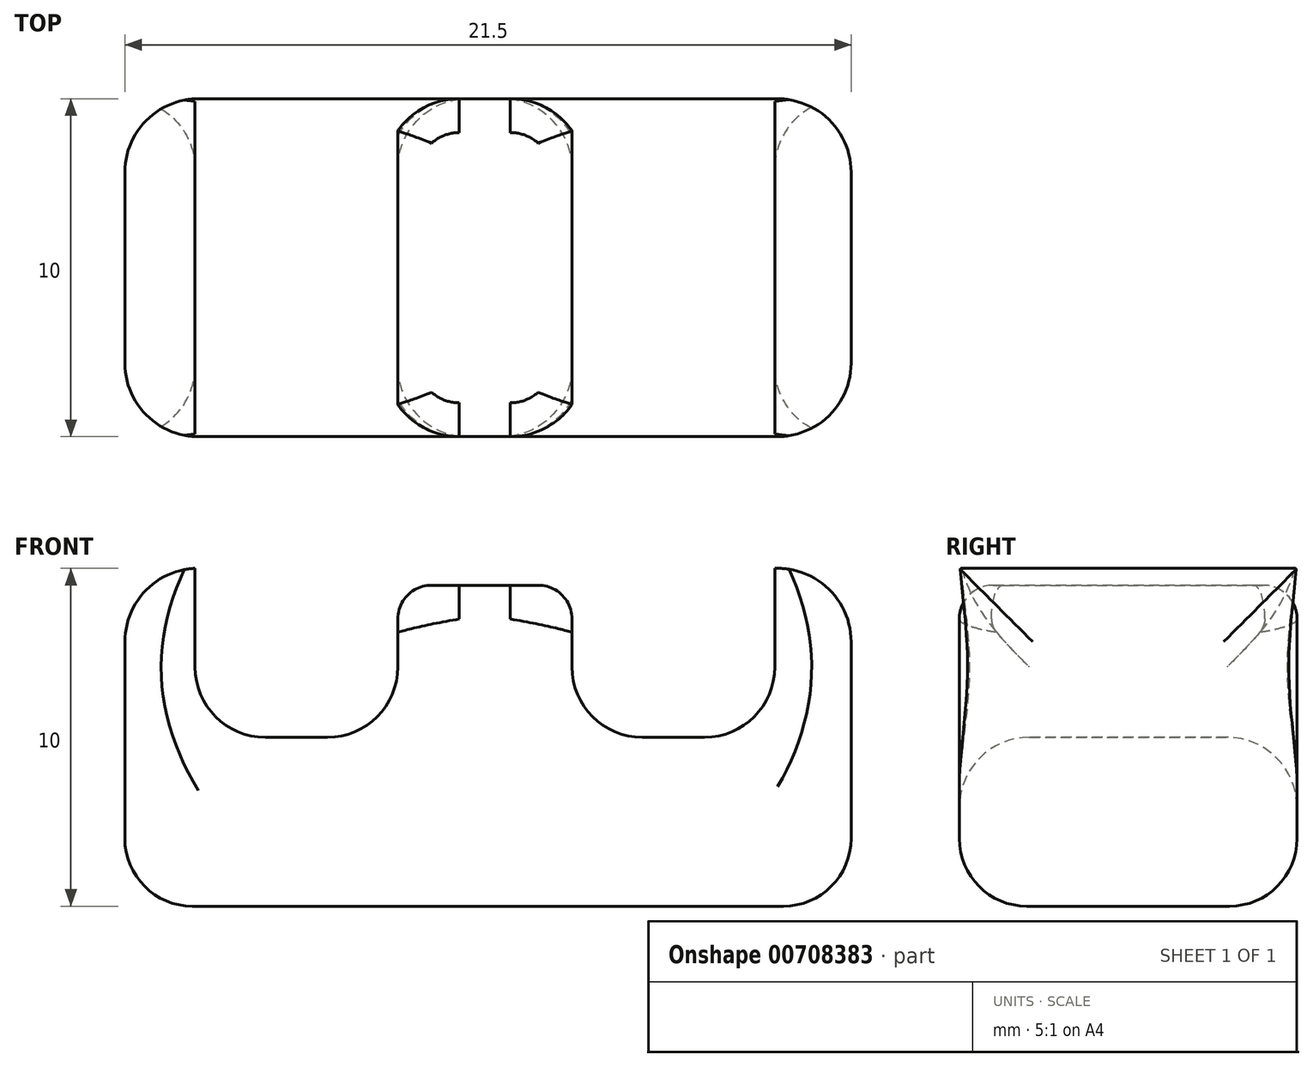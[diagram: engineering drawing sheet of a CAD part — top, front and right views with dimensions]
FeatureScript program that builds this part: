
annotation { "Feature Type Name" : "Feature", "Feature Type Description" : "" }
export const myFeature = defineFeature(function(context is Context, id is Id, definition is map)
    precondition{}
    {
        {
            var Q0;
            Q0=qCreatedBy(makeId("Top.planeOp"),FACE);
            var sketch = newSketch(context, id + "F0", { "sketchPlane" : qUnion([Q0])});
            skLineSegment(sketch, "E0.bottom", {"start": v(-10.73, 4.5) * mm, "end": v(12.77, 4.5) * mm});
            skLineSegment(sketch, "E0.top", {"start": v(-10.73, -5.5) * mm, "end": v(12.77, -5.5) * mm});
            skLineSegment(sketch, "E0.left", {"start": v(-10.73, 4.5) * mm, "end": v(-10.73, -5.5) * mm});
            skLineSegment(sketch, "E0.right", {"start": v(12.77, 4.5) * mm, "end": v(12.77, -5.5) * mm});
            skSolve(sketch);
        }
        {
            var Q0;
            Q0=makeQuery(id+"F0.imprint","IMPRINT",FACE,{"disambiguationData":[TD([[makeQuery(id+"F0.imprint","IMPRINT",EDGE,{"derivedFrom":sQuery(id+"F0.wireOp",EDGE,"E0.bottom")}),-1.0]])]});
            extrude(context, id + "F1", {"entities" : qUnion([Q0]), "depth" : 10 * mm, "offsetDistance" : 25 * mm});
        }
        {
            var Q0;
            Q0=makeQuery(id+"F1.opExtrude","SWEPT_FACE",FACE,{"disambiguationData":[OSD([sQuery(id+"F0.wireOp",EDGE,"E0.left")])]});
            extrude(context, id + "F2", {"entities" : qUnion([Q0]), "operationType" : NewBodyOperationType.REMOVE, "oppositeDirection" : true, "depth" : 2 * mm, "offsetDistance" : 25 * mm});
        }
        {
            var Q0;
            Q0=makeQuery(id+"F1.opExtrude","CAP_FACE",FACE,{"disambiguationData":[OSD([sQuery(id+"F0.wireOp",EDGE,"E0.bottom"),sQuery(id+"F0.wireOp",EDGE,"E0.top"),sQuery(id+"F0.wireOp",EDGE,"E0.left"),sQuery(id+"F0.wireOp",EDGE,"E0.right")])],"isStart":false});
            var sketch = newSketch(context, id + "F3", { "sketchPlane" : qUnion([Q0])});
            skLineSegment(sketch, "E1", {"start": v(-8.73, 1.42) * mm, "end": v(-6.73, 1.42) * mm});
            skLineSegment(sketch, "E2.bottom", {"start": v(-6.66, 4.5) * mm, "end": v(-0.66, 4.5) * mm});
            skLineSegment(sketch, "E2.top", {"start": v(-6.66, -5.5) * mm, "end": v(-0.66, -5.5) * mm});
            skLineSegment(sketch, "E2.left", {"start": v(-6.66, 4.5) * mm, "end": v(-6.66, -5.5) * mm});
            skLineSegment(sketch, "E2.right", {"start": v(-0.66, 4.5) * mm, "end": v(-0.66, -5.5) * mm});
            skSolve(sketch);
        }
        {
            var Q0;
            Q0=makeQuery(id+"F3.imprint","IMPRINT",FACE,{"disambiguationData":[TD([[makeQuery(id+"F3.imprint","IMPRINT",EDGE,{"derivedFrom":sQuery(id+"F3.wireOp",EDGE,"E2.bottom")}),-1.0]])]});
            extrude(context, id + "F4", {"entities" : qUnion([Q0]), "operationType" : NewBodyOperationType.REMOVE, "oppositeDirection" : true, "depth" : 5 * mm, "offsetDistance" : 25 * mm});
        }
        {
            var Q0;
            {var subQ0=sQuery(id+"F0.wireOp",EDGE,"E0.bottom");var subQ1=sQuery(id+"F0.wireOp",EDGE,"E0.right");var subQ2=sQuery(id+"F0.wireOp",EDGE,"E0.top");Q0=makeQuery(id+"F4.boolean.opBoolean","SPLIT",FACE,{"disambiguationData":[TD([makeQuery(id+"F1.opExtrude","SWEPT_FACE",FACE,{"disambiguationData":[OSD([subQ1])]})])],"derivedFrom":makeQuery(id+"F1.opExtrude","CAP_FACE",FACE,{"disambiguationData":[OSD([subQ0,subQ2,sQuery(id+"F0.wireOp",EDGE,"E0.left"),subQ1])],"isStart":false})});}
            var sketch = newSketch(context, id + "F5", { "sketchPlane" : qUnion([Q0])});
            skLineSegment(sketch, "E3.bottom", {"start": v(4.5, -5.5) * mm, "end": v(10.5, -5.5) * mm});
            skLineSegment(sketch, "E3.top", {"start": v(4.5, 4.5) * mm, "end": v(10.5, 4.5) * mm});
            skLineSegment(sketch, "E3.left", {"start": v(4.5, -5.5) * mm, "end": v(4.5, 4.5) * mm});
            skLineSegment(sketch, "E3.right", {"start": v(10.5, -5.5) * mm, "end": v(10.5, 4.5) * mm});
            skSolve(sketch);
        }
        {
            var Q0;
            Q0=makeQuery(id+"F5.imprint","IMPRINT",FACE,{"disambiguationData":[TD([[makeQuery(id+"F5.imprint","IMPRINT",EDGE,{"derivedFrom":sQuery(id+"F5.wireOp",EDGE,"E3.bottom")}),1.0]])]});
            extrude(context, id + "F6", {"entities" : qUnion([Q0]), "operationType" : NewBodyOperationType.REMOVE, "oppositeDirection" : true, "depth" : 5 * mm, "offsetDistance" : 25 * mm});
        }
        {
            var Q0;
            Q0=makeQuery(id+"F6.boolean.opBoolean","COPY",FACE,{"derivedFrom":makeQuery(id+"F6.opExtrude","CAP_FACE",FACE,{"disambiguationData":[OSD([sQuery(id+"F5.wireOp",EDGE,"E3.bottom"),sQuery(id+"F5.wireOp",EDGE,"E3.top"),sQuery(id+"F5.wireOp",EDGE,"E3.left"),sQuery(id+"F5.wireOp",EDGE,"E3.right")])],"isStart":false})});
            fillet(context, id + "F7", {"entities" : qUnion([Q0]), "radius" : 2.08 * mm, "tangentPropagation" : true, "allowEdgeOverflow" : false});
        }
        {
            var Q0;
            Q0=makeQuery(id+"F4.boolean.opBoolean","COPY",FACE,{"derivedFrom":makeQuery(id+"F4.opExtrude","CAP_FACE",FACE,{"disambiguationData":[OSD([sQuery(id+"F3.wireOp",EDGE,"E2.bottom"),sQuery(id+"F3.wireOp",EDGE,"E2.top"),sQuery(id+"F3.wireOp",EDGE,"E2.left"),sQuery(id+"F3.wireOp",EDGE,"E2.right")])],"isStart":false})});
            fillet(context, id + "F8", {"entities" : qUnion([Q0]), "radius" : 2.08 * mm, "tangentPropagation" : true, "allowEdgeOverflow" : false});
        }
        {
            var Q0;
            {var subQ0=sQuery(id+"F0.wireOp",EDGE,"E0.bottom");var subQ2=sQuery(id+"F0.wireOp",EDGE,"E0.top");var subQ4=makeQuery(id+"F4.opExtrude","SWEPT_FACE",FACE,{"disambiguationData":[OSD([sQuery(id+"F3.wireOp",EDGE,"E2.right")])]});var subQ5=sQuery(id+"F0.wireOp",EDGE,"E0.right");Q0=makeQuery(id+"F6.boolean.opBoolean","SPLIT",FACE,{"disambiguationData":[TD([makeQuery(id+"F4.boolean.opBoolean","COPY",FACE,{"derivedFrom":subQ4})])],"derivedFrom":makeQuery(id+"F4.boolean.opBoolean","SPLIT",FACE,{"disambiguationData":[TD([makeQuery(id+"F1.opExtrude","SWEPT_FACE",FACE,{"disambiguationData":[OSD([subQ5])]})])],"derivedFrom":makeQuery(id+"F1.opExtrude","CAP_FACE",FACE,{"disambiguationData":[OSD([subQ0,subQ2,sQuery(id+"F0.wireOp",EDGE,"E0.left"),subQ5])],"isStart":false})})});}
            extrude(context, id + "F9", {"entities" : qUnion([Q0]), "operationType" : NewBodyOperationType.REMOVE, "oppositeDirection" : true, "depth" : 0.5 * mm, "offsetDistance" : 25 * mm});
        }
        {
            var Q0;
            Q0=makeQuery(id+"F1.opExtrude","CAP_FACE",FACE,{"disambiguationData":[OSD([sQuery(id+"F0.wireOp",EDGE,"E0.bottom"),sQuery(id+"F0.wireOp",EDGE,"E0.top"),sQuery(id+"F0.wireOp",EDGE,"E0.left"),sQuery(id+"F0.wireOp",EDGE,"E0.right")])],"isStart":true});
            fillet(context, id + "F10", {"entities" : qUnion([Q0]), "radius" : 2 * mm, "tangentPropagation" : true, "allowEdgeOverflow" : false});
        }
        {
            var Q0;
            Q0=makeQuery(id+"F2.boolean.opBoolean","COPY",FACE,{"derivedFrom":makeQuery(id+"F2.opExtrude","CAP_FACE",FACE,{"disambiguationData":[OSD([sQuery(id+"F0.wireOp",EDGE,"E0.left")])],"isStart":false})});
            fillet(context, id + "F11", {"entities" : qUnion([Q0]), "radius" : 2.17 * mm, "tangentPropagation" : true, "allowEdgeOverflow" : false});
        }
        {
            var Q0;
            Q0=makeQuery(id+"F1.opExtrude","SWEPT_FACE",FACE,{"disambiguationData":[OSD([sQuery(id+"F0.wireOp",EDGE,"E0.right")])]});
            fillet(context, id + "F12", {"entities" : qUnion([Q0]), "radius" : 2.17 * mm, "tangentPropagation" : true, "allowEdgeOverflow" : false});
        }
        {
            var Q0;
            Q0=makeQuery(id+"F9.boolean.opBoolean","COPY",FACE,{"derivedFrom":makeQuery(id+"F9.opExtrude","CAP_FACE",FACE,{"disambiguationData":[OSD([sQuery(id+"F0.wireOp",EDGE,"E0.bottom"),sQuery(id+"F0.wireOp",EDGE,"E0.top"),sQuery(id+"F0.wireOp",EDGE,"E0.left"),sQuery(id+"F0.wireOp",EDGE,"E0.right")])],"isStart":false})});
            fillet(context, id + "F13", {"entities" : qUnion([Q0]), "radius" : 1 * mm, "tangentPropagation" : true, "allowEdgeOverflow" : false});
        }
    });
